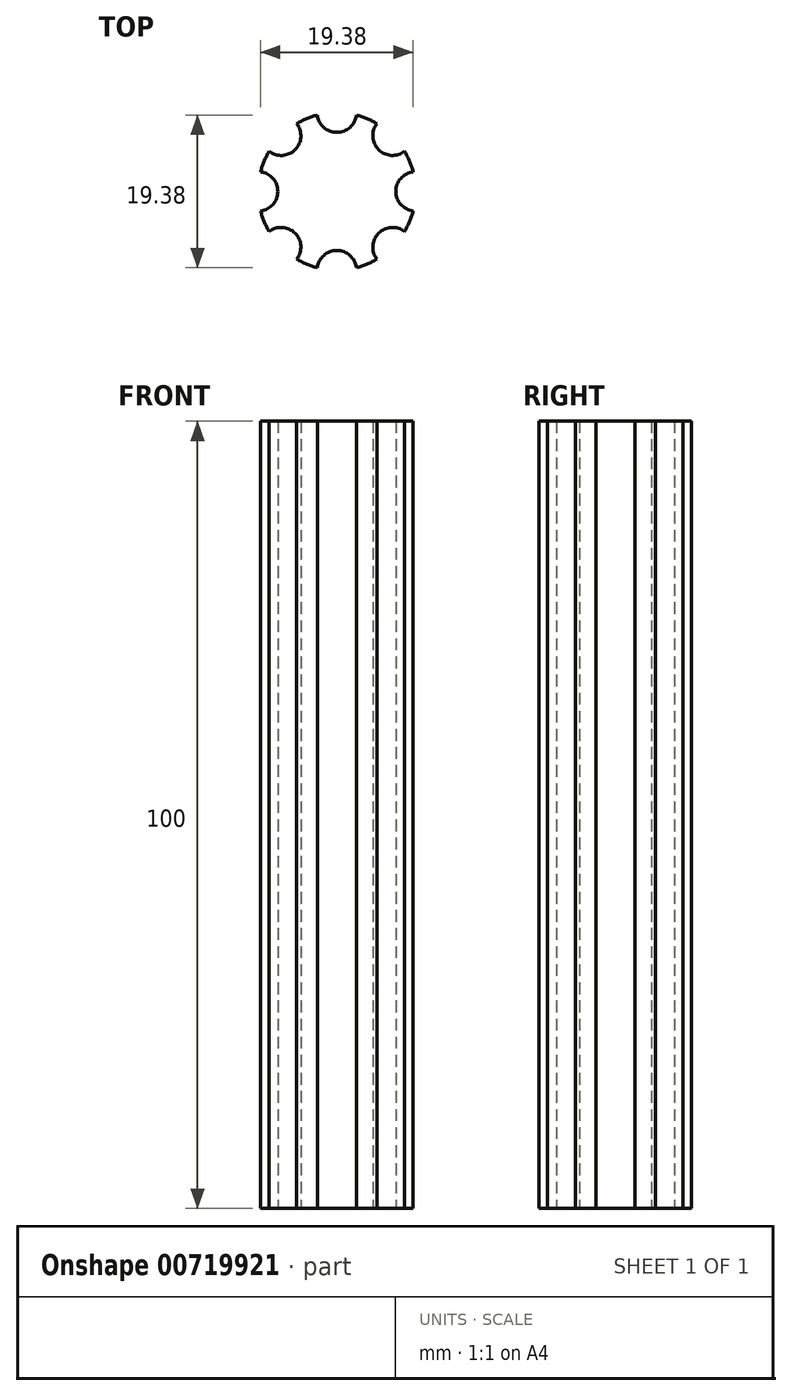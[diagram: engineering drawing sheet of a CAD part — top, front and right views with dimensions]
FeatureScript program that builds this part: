
annotation { "Feature Type Name" : "Feature", "Feature Type Description" : "" }
export const myFeature = defineFeature(function(context is Context, id is Id, definition is map)
    precondition{}
    {
        {
            var Q0;
            Q0=qCreatedBy(makeId("Top.planeOp"),FACE);
            var sketch = newSketch(context, id + "F0", { "sketchPlane" : qUnion([Q0])});
            skArc(sketch, "E0", {"start": v(5.1, 8.6) * mm, "mid": v(3.83, 9.24) * mm, "end": v(2.48, 9.69) * mm});
            skArc(sketch, "E1", {"start": v(-2.48, 9.69) * mm, "mid": v(0, 7.5) * mm, "end": v(2.48, 9.69) * mm});
            skArc(sketch, "E2.1.0", {"start": v(-8.6, 5.1) * mm, "mid": v(-5.3, 5.3) * mm, "end": v(-5.1, 8.6) * mm});
            skArc(sketch, "E2.2.0", {"start": v(-9.69, -2.48) * mm, "mid": v(-7.5, 0) * mm, "end": v(-9.69, 2.48) * mm});
            skArc(sketch, "E2.3.0", {"start": v(-5.1, -8.6) * mm, "mid": v(-5.3, -5.3) * mm, "end": v(-8.6, -5.1) * mm});
            skArc(sketch, "E2.4.0", {"start": v(2.48, -9.69) * mm, "mid": v(0, -7.5) * mm, "end": v(-2.48, -9.69) * mm});
            skArc(sketch, "E2.5.0", {"start": v(8.6, -5.1) * mm, "mid": v(5.3, -5.3) * mm, "end": v(5.1, -8.6) * mm});
            skArc(sketch, "E2.6.0", {"start": v(9.69, 2.48) * mm, "mid": v(7.5, 0) * mm, "end": v(9.69, -2.48) * mm});
            skArc(sketch, "E2.7.0", {"start": v(5.1, 8.6) * mm, "mid": v(5.3, 5.3) * mm, "end": v(8.6, 5.1) * mm});
            skArc(sketch, "E3.trimOffspring", {"start": v(9.69, 2.48) * mm, "mid": v(9.24, 3.83) * mm, "end": v(8.6, 5.1) * mm});
            skArc(sketch, "E4.trimOffspring", {"start": v(8.6, -5.1) * mm, "mid": v(9.24, -3.83) * mm, "end": v(9.69, -2.48) * mm});
            skArc(sketch, "E5.trimOffspring", {"start": v(2.48, -9.69) * mm, "mid": v(3.83, -9.24) * mm, "end": v(5.1, -8.6) * mm});
            skArc(sketch, "E6.trimOffspring", {"start": v(-5.1, -8.6) * mm, "mid": v(-3.83, -9.24) * mm, "end": v(-2.48, -9.69) * mm});
            skArc(sketch, "E7.trimOffspring", {"start": v(-9.69, -2.48) * mm, "mid": v(-9.24, -3.83) * mm, "end": v(-8.6, -5.1) * mm});
            skArc(sketch, "E8.trimOffspring", {"start": v(-8.6, 5.1) * mm, "mid": v(-9.24, 3.83) * mm, "end": v(-9.69, 2.48) * mm});
            skArc(sketch, "E9.trimOffspring", {"start": v(-2.48, 9.69) * mm, "mid": v(-3.83, 9.24) * mm, "end": v(-5.1, 8.6) * mm});
            skSolve(sketch);
        }
        {
            var Q0;
            Q0 = qSketchRegion(id + "F0", true);
            extrude(context, id + "F1", {"entities" : qUnion([Q0]), "depth" : 100 * mm, "offsetDistance" : 25 * mm});
        }
    });
